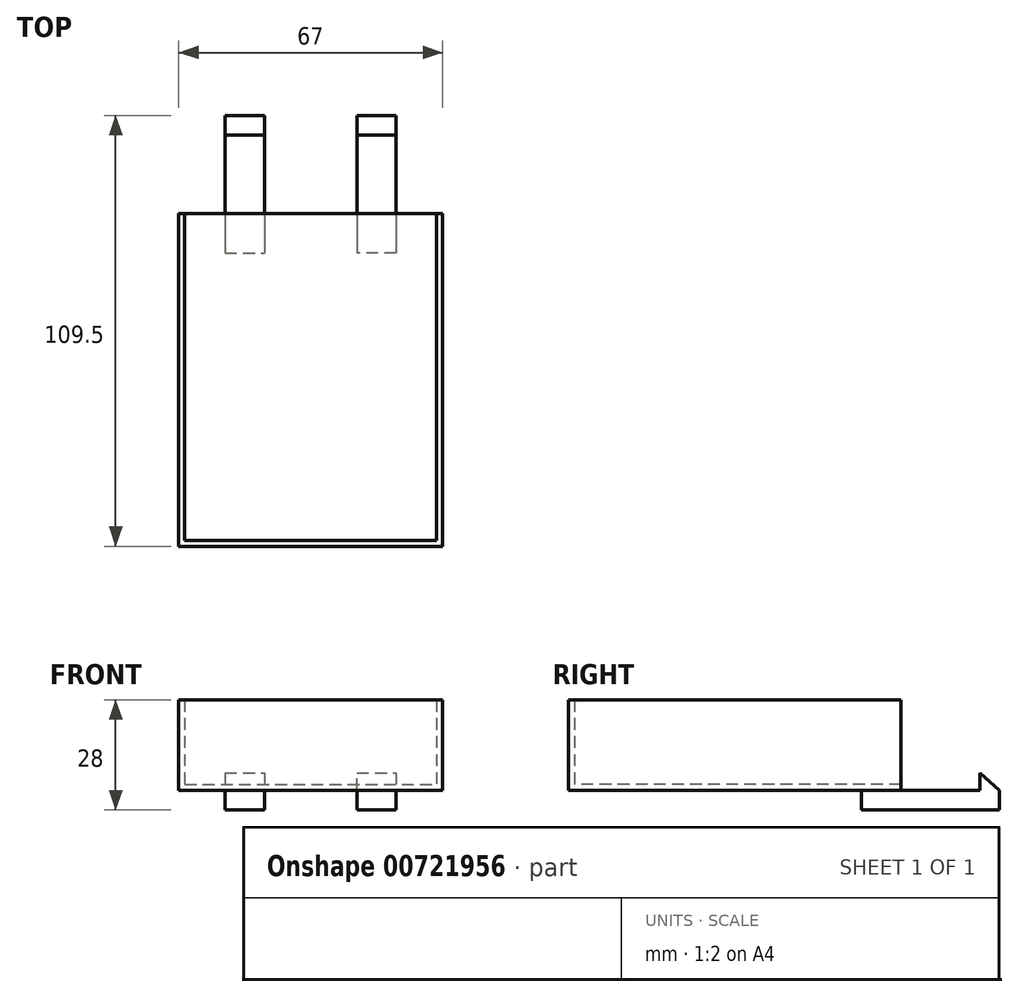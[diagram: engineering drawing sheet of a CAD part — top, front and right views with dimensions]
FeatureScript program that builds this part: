
annotation { "Feature Type Name" : "Feature", "Feature Type Description" : "" }
export const myFeature = defineFeature(function(context is Context, id is Id, definition is map)
    precondition{}
    {
        {
            var Q0;
            Q0=qCreatedBy(makeId("Top.planeOp"),FACE);
            var sketch = newSketch(context, id + "F0", { "sketchPlane" : qUnion([Q0])});
            skLineSegment(sketch, "E0.bottom", {"start": v(-33.5, 48.42) * mm, "end": v(33.5, 48.42) * mm});
            skLineSegment(sketch, "E0.top", {"start": v(-33.5, -36.08) * mm, "end": v(33.5, -36.08) * mm});
            skLineSegment(sketch, "E0.left", {"start": v(-33.5, 48.42) * mm, "end": v(-33.5, -36.08) * mm});
            skLineSegment(sketch, "E0.right", {"start": v(33.5, 48.42) * mm, "end": v(33.5, -36.08) * mm});
            skLineSegment(sketch, "E1", {"start": v(-32, 48.42) * mm, "end": v(-32, -36.08) * mm});
            skLineSegment(sketch, "E2", {"start": v(32, 48.42) * mm, "end": v(32, -36.08) * mm});
            skLineSegment(sketch, "E3", {"start": v(-32, -34.58) * mm, "end": v(32, -34.58) * mm});
            skSolve(sketch);
        }
        {
            var Q0;
            {var subQ0=sQuery(id+"F0.wireOp",EDGE,"E0.left");Q0=makeQuery(id+"F0.imprint","IMPRINT",FACE,{"disambiguationData":[TD([[makeQuery(id+"F0.imprint","IMPRINT",EDGE,{"derivedFrom":subQ0}),1.0]])]});}
            var Q1;
            {var subQ5=sQuery(id+"F0.wireOp",EDGE,"E3");Q1=makeQuery(id+"F0.imprint","IMPRINT",FACE,{"disambiguationData":[TD([[makeQuery(id+"F0.imprint","IMPRINT",EDGE,{"derivedFrom":subQ5}),-1.0]])]});}
            var Q2;
            {var subQ4=sQuery(id+"F0.wireOp",EDGE,"E0.right");Q2=makeQuery(id+"F0.imprint","IMPRINT",FACE,{"disambiguationData":[TD([[makeQuery(id+"F0.imprint","IMPRINT",EDGE,{"derivedFrom":subQ4}),-1.0]])]});}
            extrude(context, id + "F1", {"entities" : qUnion([Q0, Q1, Q2]), "depth" : 23 * mm, "offsetDistance" : 25 * mm});
        }
        {
            var Q0;
            Q0 = qSketchRegion(id + "F0", true);
            extrude(context, id + "F2", {"entities" : qUnion([Q0]), "operationType" : NewBodyOperationType.ADD, "depth" : 1.5 * mm, "offsetDistance" : 25 * mm});
        }
        {
            var Q0;
            {var subQ0=sQuery(id+"F0.wireOp",EDGE,"E0.right");var subQ1=sQuery(id+"F0.wireOp",EDGE,"E0.left");var subQ2=sQuery(id+"F0.wireOp",EDGE,"E0.top");var subQ3=sQuery(id+"F0.wireOp",EDGE,"E0.bottom");Q0=makeQuery(id+"F2.boolean.opBoolean","MERGE",FACE,{"derivedFrom":[makeQuery(id+"F1.opExtrude","CAP_FACE",FACE,{"disambiguationData":[OSD([subQ3,subQ2,subQ1,subQ0,sQuery(id+"F0.wireOp",EDGE,"E1"),sQuery(id+"F0.wireOp",EDGE,"E2"),sQuery(id+"F0.wireOp",EDGE,"E3")])],"isStart":true}),makeQuery(id+"F2.opExtrude","CAP_FACE",FACE,{"disambiguationData":[OSD([subQ3,subQ2,subQ1,subQ0])],"isStart":true})]});}
            var sketch = newSketch(context, id + "F3", { "sketchPlane" : qUnion([Q0])});
            skLineSegment(sketch, "E4.bottom", {"start": v(21.75, -48.42) * mm, "end": v(11.75, -48.42) * mm});
            skLineSegment(sketch, "E4.top", {"start": v(21.75, -38.42) * mm, "end": v(11.75, -38.42) * mm});
            skLineSegment(sketch, "E4.left", {"start": v(21.75, -48.42) * mm, "end": v(21.75, -38.42) * mm});
            skLineSegment(sketch, "E4.right", {"start": v(11.75, -48.42) * mm, "end": v(11.75, -38.42) * mm});
            skLineSegment(sketch, "E5", {"start": v(0, -48.42) * mm, "end": v(0, 36.08) * mm});
            skLineSegment(sketch, "E6.MirrorCS", {"start": v(-11.75, -48.42) * mm, "end": v(-11.75, -38.42) * mm});
            skLineSegment(sketch, "E7.MirrorCS", {"start": v(-21.75, -38.42) * mm, "end": v(-11.75, -38.42) * mm});
            skLineSegment(sketch, "E8.MirrorCS", {"start": v(-21.75, -48.42) * mm, "end": v(-21.75, -38.42) * mm});
            skLineSegment(sketch, "E9.MirrorCS", {"start": v(-21.75, -48.42) * mm, "end": v(-11.75, -48.42) * mm});
            skPoint(sketch, "E10", {"position": v(16.75, -48.42) * mm});
            skSolve(sketch);
        }
        {
            var Q0;
            Q0=makeQuery(id+"F3.imprint","IMPRINT",FACE,{"disambiguationData":[TD([[makeQuery(id+"F3.imprint","IMPRINT",EDGE,{"derivedFrom":sQuery(id+"F3.wireOp",EDGE,"E4.bottom")}),1.0]])]});
            var Q1;
            Q1=makeQuery(id+"F3.imprint","IMPRINT",FACE,{"disambiguationData":[TD([[makeQuery(id+"F3.imprint","IMPRINT",EDGE,{"derivedFrom":sQuery(id+"F3.wireOp",EDGE,"E6.MirrorCS")}),1.0]])]});
            extrude(context, id + "F4", {"entities" : qUnion([Q0, Q1]), "operationType" : NewBodyOperationType.ADD, "depth" : 5 * mm, "offsetDistance" : 25 * mm});
        }
        {
            var Q0;
            {var subQ0=sQuery(id+"F0.wireOp",EDGE,"E0.bottom");Q0=makeQuery(id+"F4.boolean.opBoolean","MERGE",FACE,{"derivedFrom":[makeQuery(id+"F2.boolean.opBoolean","MERGE",FACE,{"derivedFrom":[makeQuery(id+"F1.opExtrude","SWEPT_FACE",FACE,{"disambiguationData":[OSD([subQ0]),TDD([makeQuery(id+"F0.imprint","IMPRINT",EDGE,{"disambiguationData":[TD([[makeQuery(id+"F0.imprint","INTERSECT",VERTEX,{"derivedFrom":[subQ0,sQuery(id+"F0.wireOp",EDGE,"E0.left")]}),-1.0]])],"derivedFrom":subQ0})])]}),makeQuery(id+"F1.opExtrude","SWEPT_FACE",FACE,{"disambiguationData":[OSD([subQ0]),TDD([makeQuery(id+"F0.imprint","IMPRINT",EDGE,{"disambiguationData":[TD([[makeQuery(id+"F0.imprint","INTERSECT",VERTEX,{"derivedFrom":[subQ0,sQuery(id+"F0.wireOp",EDGE,"E0.right")]}),1.0]])],"derivedFrom":subQ0})])]}),makeQuery(id+"F2.opExtrude","SWEPT_FACE",FACE,{"disambiguationData":[OSD([subQ0])]})]}),makeQuery(id+"F4.opExtrude","SWEPT_FACE",FACE,{"disambiguationData":[OSD([sQuery(id+"F3.wireOp",EDGE,"E4.bottom")])]}),makeQuery(id+"F4.opExtrude","SWEPT_FACE",FACE,{"disambiguationData":[OSD([sQuery(id+"F3.wireOp",EDGE,"E9.MirrorCS")])]})]});}
            var sketch = newSketch(context, id + "F5", { "sketchPlane" : qUnion([Q0])});
            skLineSegment(sketch, "E11.bottom", {"start": v(-21.75, 0) * mm, "end": v(-11.75, 0) * mm});
            skLineSegment(sketch, "E11.top", {"start": v(-21.75, -5) * mm, "end": v(-11.75, -5) * mm});
            skLineSegment(sketch, "E11.left", {"start": v(-21.75, 0) * mm, "end": v(-21.75, -5) * mm});
            skLineSegment(sketch, "E11.right", {"start": v(-11.75, 0) * mm, "end": v(-11.75, -5) * mm});
            skLineSegment(sketch, "E12", {"start": v(0, 0) * mm, "end": v(0, 17.03) * mm});
            skLineSegment(sketch, "E13.MirrorCS", {"start": v(11.75, 0) * mm, "end": v(11.75, -5) * mm});
            skLineSegment(sketch, "E14.MirrorCS", {"start": v(21.75, 0) * mm, "end": v(11.75, 0) * mm});
            skLineSegment(sketch, "E15.MirrorCS", {"start": v(21.75, 0) * mm, "end": v(21.75, -5) * mm});
            skLineSegment(sketch, "E16.MirrorCS", {"start": v(21.75, -5) * mm, "end": v(11.75, -5) * mm});
            skSolve(sketch);
        }
        {
            var Q0;
            Q0=makeQuery(id+"F5.imprint","IMPRINT",FACE,{"disambiguationData":[TD([[makeQuery(id+"F5.imprint","IMPRINT",EDGE,{"derivedFrom":sQuery(id+"F5.wireOp",EDGE,"E11.bottom")}),-1.0]])]});
            var Q1;
            Q1=makeQuery(id+"F5.imprint","IMPRINT",FACE,{"disambiguationData":[TD([[makeQuery(id+"F5.imprint","IMPRINT",EDGE,{"derivedFrom":sQuery(id+"F5.wireOp",EDGE,"E13.MirrorCS")}),-1.0]])]});
            extrude(context, id + "F6", {"entities" : qUnion([Q0, Q1]), "operationType" : NewBodyOperationType.ADD, "depth" : 25 * mm, "offsetDistance" : 25 * mm});
        }
        {
            var Q0;
            Q0=makeQuery(id+"F6.opExtrude","SWEPT_FACE",FACE,{"disambiguationData":[OSD([sQuery(id+"F5.wireOp",EDGE,"E14.MirrorCS")])]});
            var sketch = newSketch(context, id + "F7", { "sketchPlane" : qUnion([Q0])});
            skLineSegment(sketch, "E17.bottom", {"start": v(-21.75, 73.42) * mm, "end": v(-11.75, 73.42) * mm});
            skLineSegment(sketch, "E17.top", {"start": v(-21.75, 68.42) * mm, "end": v(-11.75, 68.42) * mm});
            skLineSegment(sketch, "E17.left", {"start": v(-21.75, 73.42) * mm, "end": v(-21.75, 68.42) * mm});
            skLineSegment(sketch, "E17.right", {"start": v(-11.75, 73.42) * mm, "end": v(-11.75, 68.42) * mm});
            skLineSegment(sketch, "E18.MirrorCS", {"start": v(11.75, 73.42) * mm, "end": v(11.75, 68.42) * mm});
            skLineSegment(sketch, "E19.MirrorCS", {"start": v(21.75, 73.42) * mm, "end": v(11.75, 73.42) * mm});
            skLineSegment(sketch, "E20.MirrorCS", {"start": v(21.75, 73.42) * mm, "end": v(21.75, 68.42) * mm});
            skLineSegment(sketch, "E21.MirrorCS", {"start": v(21.75, 68.42) * mm, "end": v(11.75, 68.42) * mm});
            skSolve(sketch);
        }
        {
            var Q0;
            Q0=makeQuery(id+"F7.imprint","IMPRINT",FACE,{"disambiguationData":[TD([[makeQuery(id+"F7.imprint","IMPRINT",EDGE,{"derivedFrom":sQuery(id+"F7.wireOp",EDGE,"E18.MirrorCS")}),1.0]])]});
            var Q1;
            Q1=makeQuery(id+"F7.imprint","IMPRINT",FACE,{"disambiguationData":[TD([[makeQuery(id+"F7.imprint","IMPRINT",EDGE,{"derivedFrom":sQuery(id+"F7.wireOp",EDGE,"E17.bottom")}),-1.0]])]});
            extrude(context, id + "F8", {"entities" : qUnion([Q0, Q1]), "operationType" : NewBodyOperationType.ADD, "depth" : 5 * mm, "offsetDistance" : 25 * mm});
        }
        {
            var Q0;
            Q0=makeQuery(id+"F8.boolean.opBoolean","MERGE",FACE,{"derivedFrom":[makeQuery(id+"F6.boolean.opBoolean","MERGE",FACE,{"derivedFrom":[makeQuery(id+"F4.opExtrude","SWEPT_FACE",FACE,{"disambiguationData":[OSD([sQuery(id+"F3.wireOp",EDGE,"E4.left")])]}),makeQuery(id+"F6.opExtrude","SWEPT_FACE",FACE,{"disambiguationData":[OSD([sQuery(id+"F5.wireOp",EDGE,"E11.left")])]})]}),makeQuery(id+"F8.opExtrude","SWEPT_FACE",FACE,{"disambiguationData":[OSD([sQuery(id+"F7.wireOp",EDGE,"E20.MirrorCS")])]})]});
            var sketch = newSketch(context, id + "F9", { "sketchPlane" : qUnion([Q0])});
            skLineSegment(sketch, "E22.bottom", {"start": v(68.42, 5) * mm, "end": v(73.42, 5) * mm});
            skLineSegment(sketch, "E22.top", {"start": v(68.42, 0) * mm, "end": v(73.42, 0) * mm});
            skLineSegment(sketch, "E22.left", {"start": v(68.42, 5) * mm, "end": v(68.42, 0) * mm});
            skLineSegment(sketch, "E22.right", {"start": v(73.42, 5) * mm, "end": v(73.42, 0) * mm});
            skLineSegment(sketch, "E23", {"start": v(68.42, 4.5) * mm, "end": v(73.42, 0) * mm});
            skSolve(sketch);
        }
        {
            var Q0;
            {var subQ0=sQuery(id+"F9.wireOp",EDGE,"E22.bottom");Q0=makeQuery(id+"F9.imprint","IMPRINT",FACE,{"disambiguationData":[TD([[makeQuery(id+"F9.imprint","IMPRINT",EDGE,{"derivedFrom":subQ0}),1.0]])]});}
            extrude(context, id + "F10", {"entities" : qUnion([Q0]), "operationType" : NewBodyOperationType.REMOVE, "oppositeDirection" : true, "depth" : 47.7 * mm, "offsetDistance" : 25 * mm});
        }
        {
            var Q0;
            Q0=makeQuery(id+"F1.opExtrude","SWEPT_BODY",BODY,{"disambiguationData":[OSD([sQuery(id+"F0.wireOp",EDGE,"E0.bottom"),sQuery(id+"F0.wireOp",EDGE,"E0.top"),sQuery(id+"F0.wireOp",EDGE,"E0.left"),sQuery(id+"F0.wireOp",EDGE,"E0.right"),sQuery(id+"F0.wireOp",EDGE,"E1"),sQuery(id+"F0.wireOp",EDGE,"E2"),sQuery(id+"F0.wireOp",EDGE,"E3")])]});
            transform(context, id + "F11", {"entities" : qUnion([Q0]), "transformType" : TransformType.TRANSLATION_3D, "dx" : 0 * mm, "dy" : 0 * mm, "dz" : 0 * mm, "makeCopy" : true});
        }
        {
            var Q0;
            Q0=makeQuery(id+"F1.opExtrude","SWEPT_BODY",BODY,{"disambiguationData":[OSD([sQuery(id+"F0.wireOp",EDGE,"E0.bottom"),sQuery(id+"F0.wireOp",EDGE,"E0.top"),sQuery(id+"F0.wireOp",EDGE,"E0.left"),sQuery(id+"F0.wireOp",EDGE,"E0.right"),sQuery(id+"F0.wireOp",EDGE,"E1"),sQuery(id+"F0.wireOp",EDGE,"E2"),sQuery(id+"F0.wireOp",EDGE,"E3")])]});
            deleteBodies(context, id + "F12", {"entities" : qUnion([Q0])});
        }
    });
